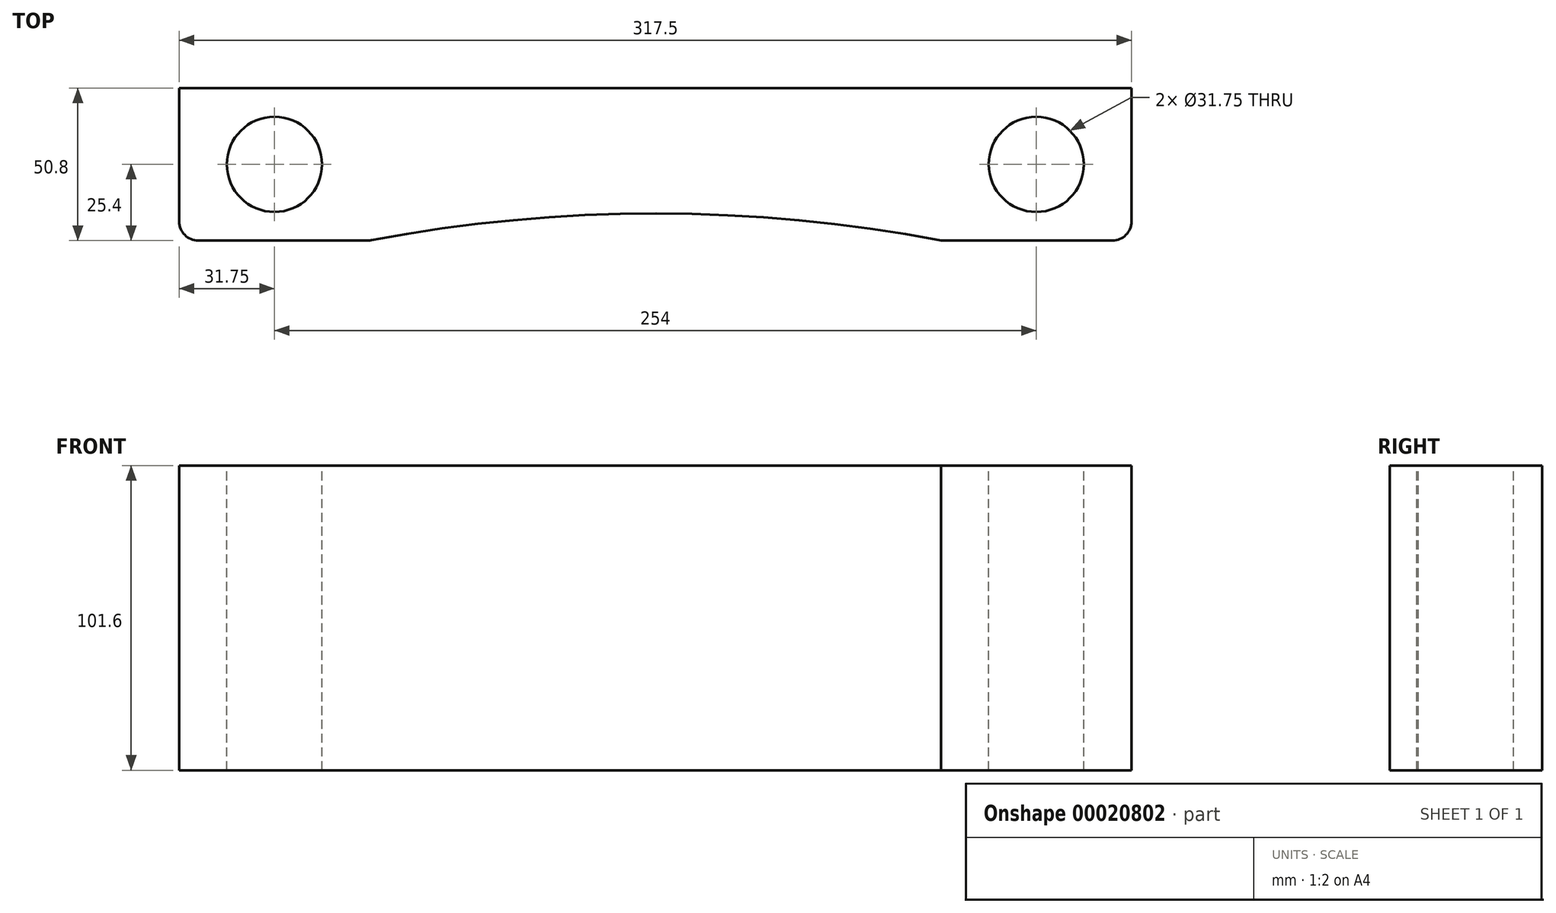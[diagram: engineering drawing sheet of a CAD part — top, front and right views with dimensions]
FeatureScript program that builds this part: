
annotation { "Feature Type Name" : "Feature", "Feature Type Description" : "" }
export const myFeature = defineFeature(function(context is Context, id is Id, definition is map)
    precondition{}
    {
        {
            var Q0;
            Q0=qCreatedBy(makeId("Front.planeOp"),FACE);
            var sketch = newSketch(context, id + "F0", { "sketchPlane" : qUnion([Q0])});
            skLineSegment(sketch, "E0.rect.bottom", {"start": v(158.75, -50.8) * mm, "end": v(-158.75, -50.8) * mm});
            skLineSegment(sketch, "E0.rect.top", {"start": v(158.75, 50.8) * mm, "end": v(-158.75, 50.8) * mm});
            skLineSegment(sketch, "E0.rect.left", {"start": v(158.75, -50.8) * mm, "end": v(158.75, 50.8) * mm});
            skLineSegment(sketch, "E0.rect.right", {"start": v(-158.75, -50.8) * mm, "end": v(-158.75, 50.8) * mm});
            skPoint(sketch, "E0.rect.middle", {"position": v(0, 0) * mm});
            skSolve(sketch);
        }
        {
            var Q0;
            Q0 = qSketchRegion(id + "F0", true);
            extrude(context, id + "F1", {"entities" : qUnion([Q0]), "depth" : 50.8 * mm});
        }
        {
            var Q0;
            Q0=makeQuery(id+"F1.opExtrude","SWEPT_FACE",FACE,{"disambiguationData":[OSD([sQuery(id+"F0.wireOp",EDGE,"E0.rect.top")])]});
            var sketch = newSketch(context, id + "F2", { "sketchPlane" : qUnion([Q0])});
            skArc(sketch, "E1", {"start": v(95.25, -50.8) * mm, "mid": v(0, -41.8) * mm, "end": v(-95.25, -50.8) * mm});
            skSolve(sketch);
        }
        {
            var Q0;
            {var subQ1=sQuery(id+"F2.wireOp",EDGE,"E1");Q0=makeQuery(id+"F2.imprint","IMPRINT",FACE,{"disambiguationData":[TD([[makeQuery(id+"F2.imprint","IMPRINT",EDGE,{"derivedFrom":subQ1}),1.0]])]});}
            extrude(context, id + "F3", {"entities" : qUnion([Q0]), "operationType" : NewBodyOperationType.REMOVE, "endBound" : BoundingType.THROUGH_ALL, "oppositeDirection" : true, "depth" : 25.4 * mm});
        }
        {
            var Q0;
            Q0=makeQuery(id+"F1.opExtrude","SWEPT_FACE",FACE,{"disambiguationData":[OSD([sQuery(id+"F0.wireOp",EDGE,"E0.rect.top")])]});
            var sketch = newSketch(context, id + "F4", { "sketchPlane" : qUnion([Q0])});
            skCircle(sketch, "E2", {"center": v(-127, -25.4) * mm, "radius": 15.88 * mm});
            skCircle(sketch, "E3", {"center": v(127, -25.4) * mm, "radius": 15.88 * mm});
            skLineSegment(sketch, "E4", {"start": v(-127, -25.4) * mm, "end": v(-158.75, -25.4) * mm, "construction": true});
            skLineSegment(sketch, "E5", {"start": v(127, -25.4) * mm, "end": v(158.75, -25.4) * mm, "construction": true});
            skSolve(sketch);
        }
        {
            var Q0;
            Q0 = qSketchRegion(id + "F4", true);
            extrude(context, id + "F5", {"entities" : qUnion([Q0]), "operationType" : NewBodyOperationType.REMOVE, "endBound" : BoundingType.THROUGH_ALL, "oppositeDirection" : true, "depth" : 25.4 * mm});
        }
        {
            var Q0;
            Q0=makeQuery(id+"F1.opExtrude","CAP_EDGE",EDGE,{"disambiguationData":[OSD([sQuery(id+"F0.wireOp",EDGE,"E0.rect.left")])],"isStart":false});
            var Q1;
            Q1=makeQuery(id+"F1.opExtrude","CAP_EDGE",EDGE,{"disambiguationData":[OSD([sQuery(id+"F0.wireOp",EDGE,"E0.rect.right")])],"isStart":false});
            var Q2;
            {var subQ0=sQuery(id+"F2.wireOp",EDGE,"E1");var subQ1=sQuery(id+"F0.wireOp",EDGE,"E0.rect.top");Q2=makeQuery(id+"F3.boolean.opBoolean","COPY",EDGE,{"derivedFrom":makeQuery(id+"F3.opExtrude","SWEPT_EDGE",EDGE,{"disambiguationData":[OSD([subQ1,subQ0]),TDD([makeQuery(id+"F2.imprint","INTERSECT",VERTEX,{"disambiguationData":[OD(0.0)],"derivedFrom":[makeQuery(id+"F1.opExtrude","CAP_EDGE",EDGE,{"disambiguationData":[OSD([subQ1])],"isStart":false}),subQ0]})])]})});}
            var Q3;
            {var subQ0=sQuery(id+"F2.wireOp",EDGE,"E1");var subQ1=sQuery(id+"F0.wireOp",EDGE,"E0.rect.top");Q3=makeQuery(id+"F3.boolean.opBoolean","COPY",EDGE,{"derivedFrom":makeQuery(id+"F3.opExtrude","SWEPT_EDGE",EDGE,{"disambiguationData":[OSD([subQ1,subQ0]),TDD([makeQuery(id+"F2.imprint","INTERSECT",VERTEX,{"disambiguationData":[OD(1.0)],"derivedFrom":[makeQuery(id+"F1.opExtrude","CAP_EDGE",EDGE,{"disambiguationData":[OSD([subQ1])],"isStart":false}),subQ0]})])]})});}
            fillet(context, id + "F6", {"entities" : qUnion([Q0, Q1, Q2, Q3]), "radius" : 6.35 * mm, "tangentPropagation" : true, "allowEdgeOverflow" : false});
        }
    });
